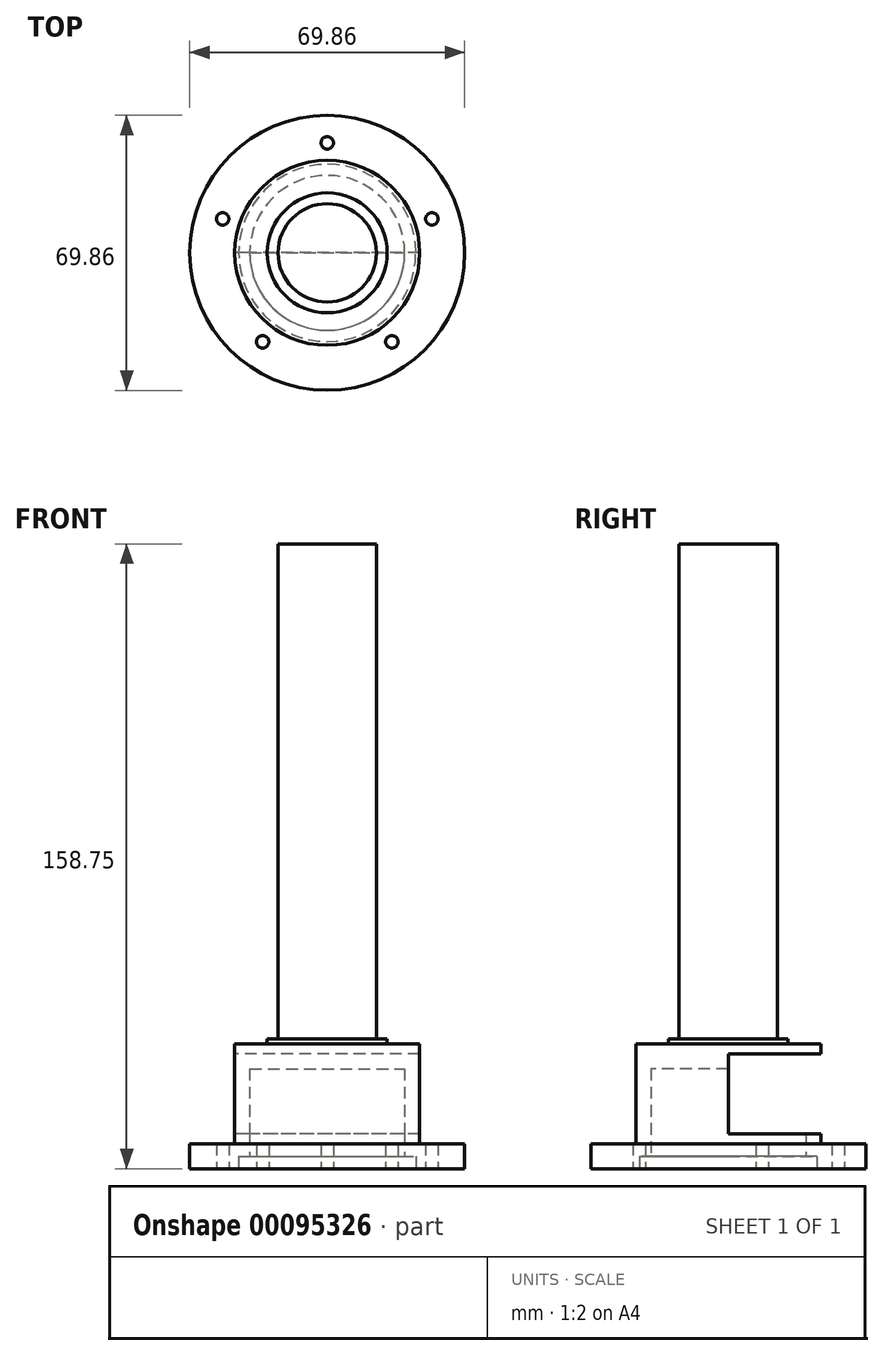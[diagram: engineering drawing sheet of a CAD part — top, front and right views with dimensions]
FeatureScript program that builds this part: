
annotation { "Feature Type Name" : "Feature", "Feature Type Description" : "" }
export const myFeature = defineFeature(function(context is Context, id is Id, definition is map)
    precondition{}
    {
        {
            var Q0;
            Q0=qCreatedBy(makeId("Top.planeOp"),FACE);
            var sketch = newSketch(context, id + "F0", { "sketchPlane" : qUnion([Q0])});
            skCircle(sketch, "E0", {"center": v(0, 0) * mm, "radius": 34.93 * mm});
            skCircle(sketch, "E1", {"center": v(0, 27.94) * mm, "radius": 1.59 * mm});
            skCircle(sketch, "E2.1.0", {"center": v(-26.57, 8.63) * mm, "radius": 1.59 * mm});
            skCircle(sketch, "E2.2.0", {"center": v(-16.42, -22.6) * mm, "radius": 1.59 * mm});
            skCircle(sketch, "E2.3.0", {"center": v(16.42, -22.6) * mm, "radius": 1.59 * mm});
            skCircle(sketch, "E2.4.0", {"center": v(26.57, 8.63) * mm, "radius": 1.59 * mm});
            skSolve(sketch);
        }
        {
            var Q0;
            Q0=makeQuery(id+"F0.imprint","IMPRINT",FACE,{"disambiguationData":[TD([[makeQuery(id+"F0.imprint","IMPRINT",EDGE,{"derivedFrom":sQuery(id+"F0.wireOp",EDGE,"E0")}),1.0]])]});
            extrude(context, id + "F1", {"entities" : qUnion([Q0]), "depth" : 6.35 * mm});
        }
        {
            var Q0;
            Q0=makeQuery(id+"F1.opExtrude","CAP_FACE",FACE,{"disambiguationData":[OSD([sQuery(id+"F0.wireOp",EDGE,"E0"),sQuery(id+"F0.wireOp",EDGE,"E1"),sQuery(id+"F0.wireOp",EDGE,"E2.1.0"),sQuery(id+"F0.wireOp",EDGE,"E2.2.0"),sQuery(id+"F0.wireOp",EDGE,"E2.3.0"),sQuery(id+"F0.wireOp",EDGE,"E2.4.0")])],"isStart":true});
            var sketch = newSketch(context, id + "F2", { "sketchPlane" : qUnion([Q0])});
            skCircle(sketch, "E3", {"center": v(0, 0) * mm, "radius": 22.5 * mm});
            skSolve(sketch);
        }
        {
            var Q0;
            Q0=makeQuery(id+"F2.imprint","IMPRINT",FACE,{"disambiguationData":[TD([[makeQuery(id+"F2.imprint","IMPRINT",EDGE,{"derivedFrom":sQuery(id+"F2.wireOp",EDGE,"E3")}),1.0]])]});
            extrude(context, id + "F3", {"entities" : qUnion([Q0]), "operationType" : NewBodyOperationType.REMOVE, "oppositeDirection" : true, "depth" : 3.17 * mm});
        }
        {
            var Q0;
            Q0=makeQuery(id+"F3.boolean.opBoolean","COPY",FACE,{"derivedFrom":makeQuery(id+"F3.opExtrude","CAP_FACE",FACE,{"disambiguationData":[OSD([sQuery(id+"F2.wireOp",EDGE,"E3")])],"isStart":false})});
            var sketch = newSketch(context, id + "F4", { "sketchPlane" : qUnion([Q0])});
            skCircle(sketch, "E4", {"center": v(0, 0) * mm, "radius": 19.69 * mm});
            skSolve(sketch);
        }
        {
            var Q0;
            Q0=makeQuery(id+"F4.imprint","IMPRINT",FACE,{"disambiguationData":[TD([[makeQuery(id+"F4.imprint","IMPRINT",EDGE,{"derivedFrom":sQuery(id+"F4.wireOp",EDGE,"E4")}),1.0]])]});
            extrude(context, id + "F5", {"entities" : qUnion([Q0]), "operationType" : NewBodyOperationType.REMOVE, "endBound" : BoundingType.THROUGH_ALL, "oppositeDirection" : true, "depth" : 25.4 * mm});
        }
        {
            var Q0;
            Q0=makeQuery(id+"F1.opExtrude","CAP_FACE",FACE,{"disambiguationData":[OSD([sQuery(id+"F0.wireOp",EDGE,"E0"),sQuery(id+"F0.wireOp",EDGE,"E1"),sQuery(id+"F0.wireOp",EDGE,"E2.1.0"),sQuery(id+"F0.wireOp",EDGE,"E2.2.0"),sQuery(id+"F0.wireOp",EDGE,"E2.3.0"),sQuery(id+"F0.wireOp",EDGE,"E2.4.0")])],"isStart":false});
            var sketch = newSketch(context, id + "F6", { "sketchPlane" : qUnion([Q0])});
            skCircle(sketch, "E5", {"center": v(0, 0) * mm, "radius": 23.5 * mm});
            skCircle(sketch, "E6.0", {"center": v(0, 0) * mm, "radius": 19.69 * mm});
            skSolve(sketch);
        }
        {
            var Q0;
            Q0=makeQuery(id+"F6.imprint","IMPRINT",FACE,{"disambiguationData":[TD([[makeQuery(id+"F6.imprint","IMPRINT",EDGE,{"derivedFrom":sQuery(id+"F6.wireOp",EDGE,"E5")}),1.0]])]});
            extrude(context, id + "F7", {"entities" : qUnion([Q0]), "operationType" : NewBodyOperationType.ADD, "depth" : 19.05 * mm});
        }
        {
            var Q0;
            Q0=makeQuery(id+"F7.opExtrude","CAP_FACE",FACE,{"disambiguationData":[OSD([sQuery(id+"F6.wireOp",EDGE,"E5"),sQuery(id+"F6.wireOp",EDGE,"E6.0")])],"isStart":false});
            var sketch = newSketch(context, id + "F8", { "sketchPlane" : qUnion([Q0])});
            skCircle(sketch, "E7.0", {"center": v(0, 0) * mm, "radius": 23.5 * mm});
            skSolve(sketch);
        }
        {
            var Q0;
            Q0 = qSketchRegion(id + "F8", true);
            extrude(context, id + "F9", {"entities" : qUnion([Q0]), "operationType" : NewBodyOperationType.ADD, "depth" : 6.35 * mm});
        }
        {
            var Q0;
            Q0=makeQuery(id+"F9.opExtrude","CAP_FACE",FACE,{"disambiguationData":[OSD([sQuery(id+"F8.wireOp",EDGE,"E7.0")])],"isStart":false});
            var sketch = newSketch(context, id + "F10", { "sketchPlane" : qUnion([Q0])});
            skCircle(sketch, "E8", {"center": v(0, 0) * mm, "radius": 12.5 * mm});
            skSolve(sketch);
        }
        {
            var Q0;
            Q0=makeQuery(id+"F10.imprint","IMPRINT",FACE,{"disambiguationData":[TD([[makeQuery(id+"F10.imprint","IMPRINT",EDGE,{"derivedFrom":sQuery(id+"F10.wireOp",EDGE,"E8")}),1.0]])]});
            extrude(context, id + "F11", {"entities" : qUnion([Q0]), "operationType" : NewBodyOperationType.ADD, "depth" : 127 * mm});
        }
        {
            var Q0;
            Q0=makeQuery(id+"F9.opExtrude","CAP_FACE",FACE,{"disambiguationData":[OSD([sQuery(id+"F8.wireOp",EDGE,"E7.0")])],"isStart":false});
            var sketch = newSketch(context, id + "F12", { "sketchPlane" : qUnion([Q0])});
            skCircle(sketch, "E9", {"center": v(0, 0) * mm, "radius": 15.24 * mm});
            skSolve(sketch);
        }
        {
            var Q0;
            Q0=makeQuery(id+"F12.imprint","IMPRINT",FACE,{"disambiguationData":[TD([[makeQuery(id+"F12.imprint","IMPRINT",EDGE,{"derivedFrom":sQuery(id+"F12.wireOp",EDGE,"E9")}),1.0]])]});
            extrude(context, id + "F13", {"entities" : qUnion([Q0]), "operationType" : NewBodyOperationType.ADD, "depth" : 1.27 * mm});
        }
        {
            var Q0;
            Q0=qCreatedBy(makeId("Front.planeOp"),FACE);
            var sketch = newSketch(context, id + "F14", { "sketchPlane" : qUnion([Q0])});
            skLineSegment(sketch, "E10", {"start": v(23.5, 31.75) * mm, "end": v(23.5, 6.35) * mm, "construction": true});
            skLineSegment(sketch, "E11", {"start": v(-23.5, 6.35) * mm, "end": v(-23.5, 31.75) * mm, "construction": true});
            skLineSegment(sketch, "E12.0", {"start": v(-34.93, 6.35) * mm, "end": v(34.93, 6.35) * mm, "construction": true});
            skLineSegment(sketch, "E13.0", {"start": v(-23.5, 31.75) * mm, "end": v(23.5, 31.75) * mm, "construction": true});
            skLineSegment(sketch, "E14.bottom", {"start": v(23.5, 8.9) * mm, "end": v(-23.5, 8.9) * mm});
            skLineSegment(sketch, "E14.top", {"start": v(23.5, 29.21) * mm, "end": v(-23.5, 29.21) * mm});
            skLineSegment(sketch, "E14.left", {"start": v(23.5, 8.9) * mm, "end": v(23.5, 29.21) * mm});
            skLineSegment(sketch, "E14.right", {"start": v(-23.5, 8.9) * mm, "end": v(-23.5, 29.21) * mm});
            skPoint(sketch, "E14.middle", {"position": v(0, 19.05) * mm});
            skPoint(sketch, "E14.middle.positionSnap0", {"position": v(23.5, 19.05) * mm});
            skPoint(sketch, "E14.centerSnap0", {"position": v(23.5, 19.05) * mm});
            skSolve(sketch);
        }
        {
            var Q0;
            Q0 = qSketchRegion(id + "F14", true);
            extrude(context, id + "F15", {"entities" : qUnion([Q0]), "operationType" : NewBodyOperationType.REMOVE, "oppositeDirection" : true, "depth" : 25.4 * mm});
        }
    });
